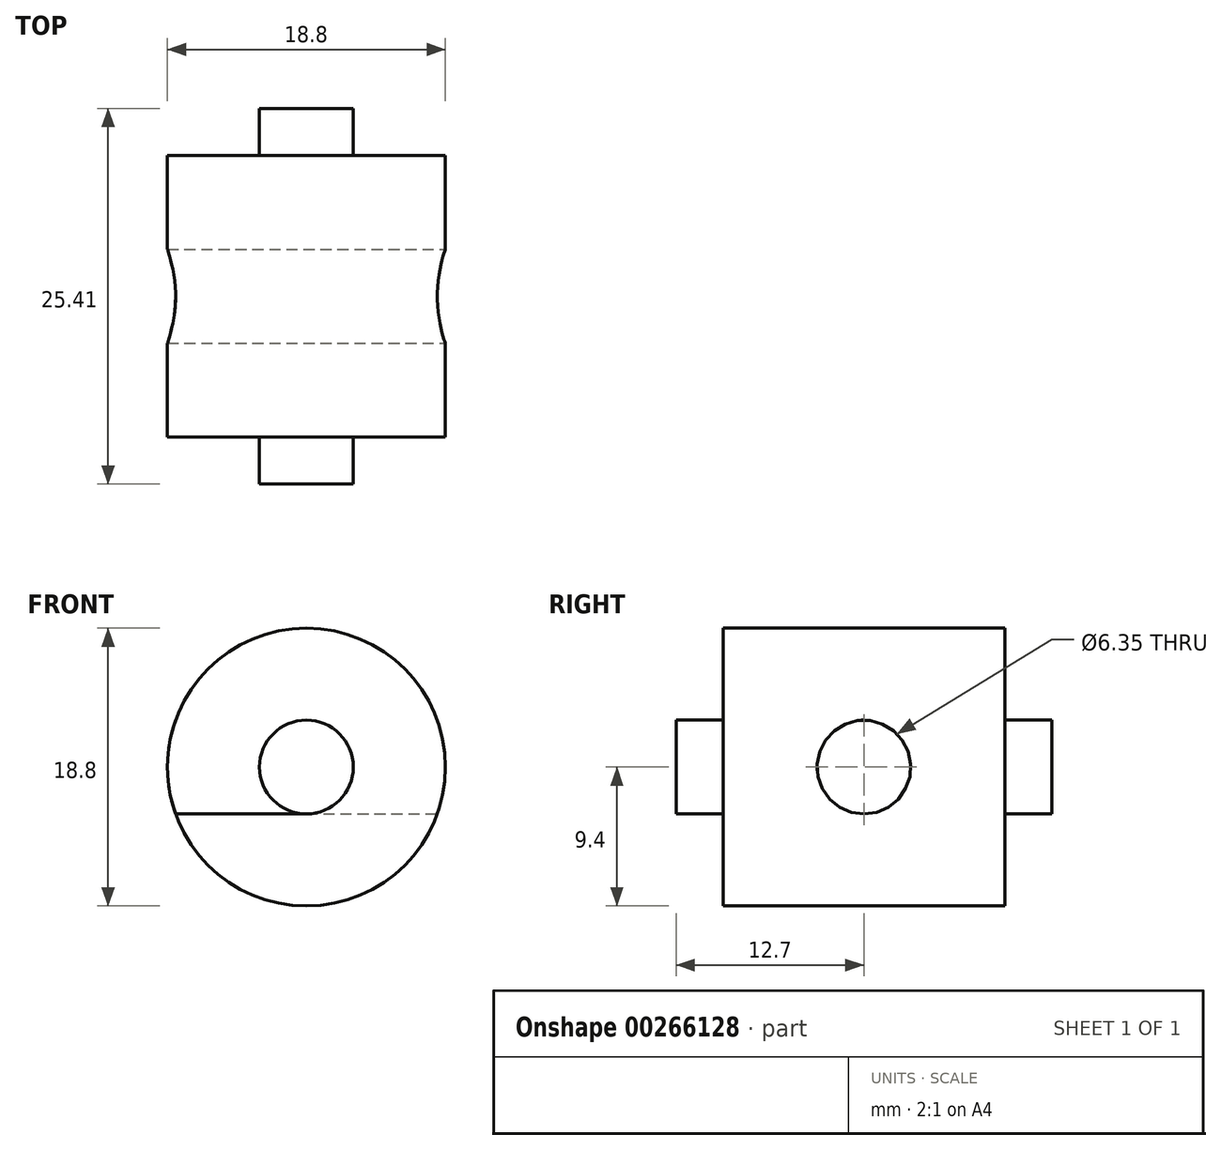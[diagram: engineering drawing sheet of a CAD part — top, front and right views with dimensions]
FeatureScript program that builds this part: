
annotation { "Feature Type Name" : "Feature", "Feature Type Description" : "" }
export const myFeature = defineFeature(function(context is Context, id is Id, definition is map)
    precondition{}
    {
        {
            var Q0;
            Q0=qCreatedBy(makeId("Front.planeOp"),FACE);
            var sketch = newSketch(context, id + "F0", { "sketchPlane" : qUnion([Q0])});
            skCircle(sketch, "E0", {"center": v(0, 0) * mm, "radius": 9.4 * mm});
            skSolve(sketch);
        }
        {
            var Q0;
            Q0 = qSketchRegion(id + "F0", true);
            var Q1;
            Q1=makeQuery(id+"F0.imprint","IMPRINT",FACE,{"disambiguationData":[TD([[makeQuery(id+"F0.imprint","IMPRINT",EDGE,{"derivedFrom":sQuery(id+"F0.wireOp",EDGE,"E0")}),1.0]])]});
            extrude(context, id + "F1", {"entities" : qUnion([Q0, Q1]), "depth" : 19.05 * mm});
        }
        {
            var Q0;
            Q0=makeQuery(id+"F1.opExtrude","CAP_FACE",FACE,{"disambiguationData":[OSD([sQuery(id+"F0.wireOp",EDGE,"E0")])],"isStart":false});
            var sketch = newSketch(context, id + "F2", { "sketchPlane" : qUnion([Q0])});
            skCircle(sketch, "E1", {"center": v(0, 0) * mm, "radius": 3.18 * mm});
            skSolve(sketch);
        }
        {
            var Q0;
            Q0 = qSketchRegion(id + "F2", true);
            extrude(context, id + "F3", {"entities" : qUnion([Q0]), "operationType" : NewBodyOperationType.ADD, "depth" : 3.17 * mm});
        }
        {
            var Q0;
            Q0=makeQuery(id+"F1.opExtrude","CAP_FACE",FACE,{"disambiguationData":[OSD([sQuery(id+"F0.wireOp",EDGE,"E0")])],"isStart":true});
            var sketch = newSketch(context, id + "F4", { "sketchPlane" : qUnion([Q0])});
            skCircle(sketch, "E2", {"center": v(0, 0) * mm, "radius": 3.18 * mm});
            skSolve(sketch);
        }
        {
            var Q0;
            Q0 = qSketchRegion(id + "F4", true);
            extrude(context, id + "F5", {"entities" : qUnion([Q0]), "operationType" : NewBodyOperationType.ADD, "depth" : 3.17 * mm});
        }
        {
            var Q0;
            Q0=qCreatedBy(makeId("Right.planeOp"),FACE);
            var sketch = newSketch(context, id + "F6", { "sketchPlane" : qUnion([Q0])});
            skLineSegment(sketch, "E3", {"start": v(0, 0) * mm, "end": v(-19.06, 0) * mm, "construction": true});
            skCircle(sketch, "E4", {"center": v(-9.53, 0) * mm, "radius": 3.18 * mm});
            skSolve(sketch);
        }
        {
            var Q0;
            Q0 = qSketchRegion(id + "F6", true);
            extrude(context, id + "F7", {"entities" : qUnion([Q0]), "operationType" : NewBodyOperationType.REMOVE, "oppositeDirection" : true, "depth" : 127 * mm});
        }
        {
            var Q0;
            Q0=qCreatedBy(makeId("Right.planeOp"),FACE);
            var sketch = newSketch(context, id + "F8", { "sketchPlane" : qUnion([Q0])});
            skLineSegment(sketch, "E5", {"start": v(-19.07, 0) * mm, "end": v(0, 0) * mm, "construction": true});
            skCircle(sketch, "E6", {"center": v(-9.53, 0) * mm, "radius": 3.18 * mm});
            skSolve(sketch);
        }
        {
            var Q0;
            Q0 = qSketchRegion(id + "F8", true);
            extrude(context, id + "F9", {"entities" : qUnion([Q0]), "operationType" : NewBodyOperationType.REMOVE, "oppositeDirection" : true, "depth" : 127 * mm});
        }
        {
            var Q0;
            Q0 = qSketchRegion(id + "F6", true);
            extrude(context, id + "F10", {"entities" : qUnion([Q0]), "operationType" : NewBodyOperationType.REMOVE, "oppositeDirection" : true, "depth" : 25.4 * mm});
        }
        {
            var Q0;
            Q0 = qSketchRegion(id + "F6", true);
            extrude(context, id + "F11", {"entities" : qUnion([Q0]), "operationType" : NewBodyOperationType.REMOVE, "oppositeDirection" : true, "depth" : 25.4 * mm, "hasSecondDirection" : true, "secondDirectionOppositeDirection" : false, "secondDirectionDepth" : 25.4 * mm});
        }
    });
